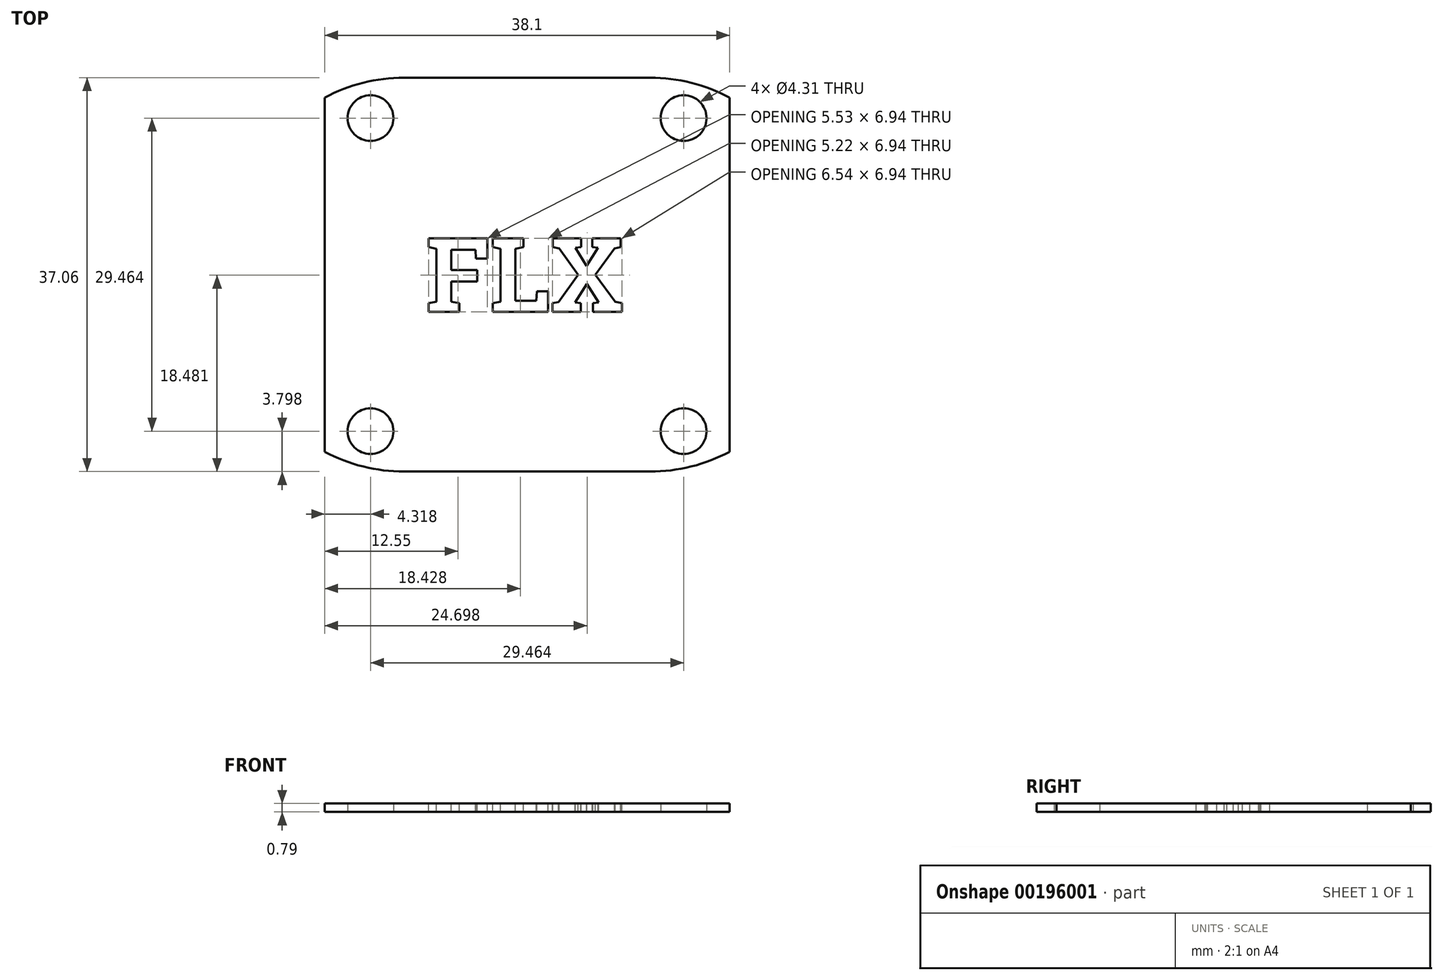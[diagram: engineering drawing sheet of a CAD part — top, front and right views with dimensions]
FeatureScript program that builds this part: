
annotation { "Feature Type Name" : "Feature", "Feature Type Description" : "" }
export const myFeature = defineFeature(function(context is Context, id is Id, definition is map)
    precondition{}
    {
        {
            var Q0;
            Q0=qCreatedBy(makeId("Top.planeOp"),FACE);
            var sketch = newSketch(context, id + "F0", { "sketchPlane" : qUnion([Q0])});
            skLineSegment(sketch, "E0", {"start": v(-19.05, 0) * mm, "end": v(-19.05, 16.67) * mm});
            skLineSegment(sketch, "E1", {"start": v(19.05, 0) * mm, "end": v(19.05, 16.67) * mm});
            skArc(sketch, "E2", {"start": v(-11.58, 18.53) * mm, "mid": v(-15.43, 18.06) * mm, "end": v(-19.05, 16.67) * mm});
            skArc(sketch, "E3", {"start": v(19.05, 16.67) * mm, "mid": v(15.43, 18.06) * mm, "end": v(11.58, 18.53) * mm});
            skLineSegment(sketch, "E4", {"start": v(-11.58, 18.53) * mm, "end": v(0, 18.53) * mm});
            skLineSegment(sketch, "E5", {"start": v(0, 18.53) * mm, "end": v(11.58, 18.53) * mm});
            skLineSegment(sketch, "E6", {"start": v(-39.62, 0) * mm, "end": v(36.58, 0) * mm, "construction": true});
            skLineSegment(sketch, "E7.MirrorCS", {"start": v(-19.05, 0) * mm, "end": v(-19.05, -16.67) * mm});
            skLineSegment(sketch, "E8.MirrorCS", {"start": v(19.05, 0) * mm, "end": v(19.05, -16.67) * mm});
            skLineSegment(sketch, "E9.MirrorCS", {"start": v(-11.58, -18.53) * mm, "end": v(0, -18.53) * mm});
            skLineSegment(sketch, "E10.MirrorCS", {"start": v(0, -18.53) * mm, "end": v(11.58, -18.53) * mm});
            skArc(sketch, "E11.MirrorCS", {"start": v(-11.58, -18.53) * mm, "mid": v(-15.43, -18.06) * mm, "end": v(-19.05, -16.67) * mm});
            skArc(sketch, "E12.MirrorCS", {"start": v(19.05, -16.67) * mm, "mid": v(15.43, -18.06) * mm, "end": v(11.58, -18.53) * mm});
            skCircle(sketch, "E13", {"center": v(-14.73, 14.73) * mm, "radius": 2.15 * mm});
            skCircle(sketch, "E14.MirrorC", {"center": v(-14.73, -14.73) * mm, "radius": 2.15 * mm});
            skLineSegment(sketch, "E15", {"start": v(0, 16.68) * mm, "end": v(0, -10.48) * mm, "construction": true});
            skCircle(sketch, "E16.MirrorC", {"center": v(14.73, 14.73) * mm, "radius": 2.15 * mm});
            skCircle(sketch, "E17.MirrorC", {"center": v(14.73, -14.73) * mm, "radius": 2.15 * mm});
            skSolve(sketch);
        }
        {
            var Q0;
            Q0=qSketchRegion(id+"F0",true);
            extrude(context, id + "F1", {"entities" : qUnion([Q0]), "depth" : 0.8 * mm});
        }
        {
            var Q0;
            Q0=makeQuery(id+"F1.opExtrude","CAP_FACE",FACE,{"disambiguationData":[OSD([sQuery(id+"F0.wireOp",EDGE,"E0"),sQuery(id+"F0.wireOp",EDGE,"E1"),sQuery(id+"F0.wireOp",EDGE,"E2"),sQuery(id+"F0.wireOp",EDGE,"E3"),sQuery(id+"F0.wireOp",EDGE,"E4"),sQuery(id+"F0.wireOp",EDGE,"E5"),sQuery(id+"F0.wireOp",EDGE,"E7.MirrorCS"),sQuery(id+"F0.wireOp",EDGE,"E8.MirrorCS"),sQuery(id+"F0.wireOp",EDGE,"E9.MirrorCS"),sQuery(id+"F0.wireOp",EDGE,"E10.MirrorCS"),sQuery(id+"F0.wireOp",EDGE,"E11.MirrorCS"),sQuery(id+"F0.wireOp",EDGE,"E12.MirrorCS"),sQuery(id+"F0.wireOp",EDGE,"E14.MirrorC"),sQuery(id+"F0.wireOp",EDGE,"E13"),sQuery(id+"F0.wireOp",EDGE,"E16.MirrorC"),sQuery(id+"F0.wireOp",EDGE,"E17.MirrorC")])],"isStart":false});
            var sketch = newSketch(context, id + "F2", { "sketchPlane" : qUnion([Q0])});
            skText(sketch, "E18", { "text": "FLX", "fontName": "RobotoSlab-Bold.ttf"});
            skLineSegment(sketch, "E19", {"start": v(9.52, 0) * mm, "end": v(-9.53, 0) * mm, "construction": true});
            const initialGuessF2  = {"E18": [-0.00953, -0.00352, 1, 0, 0.00703]};
            skSetInitialGuess(sketch, initialGuessF2);
            skSolve(sketch);
        }
        {
            var Q0;
            Q0=makeQuery(id+"F2.imprint","IMPRINT",FACE,{"disambiguationData":[TD([[makeQuery(id+"F2.imprint","IMPRINT",EDGE,{"derivedFrom":sQuery(id+"F2.wireOp",EDGE,"E18.sketch_text.stroke-34")}),-1.0]])]});
            var Q1;
            Q1=makeQuery(id+"F2.imprint","IMPRINT",FACE,{"disambiguationData":[TD([[makeQuery(id+"F2.imprint","IMPRINT",EDGE,{"derivedFrom":sQuery(id+"F2.wireOp",EDGE,"E18.sketch_text.stroke-18")}),-1.0]])]});
            var Q2;
            Q2=makeQuery(id+"F2.imprint","IMPRINT",FACE,{"disambiguationData":[TD([[makeQuery(id+"F2.imprint","IMPRINT",EDGE,{"derivedFrom":sQuery(id+"F2.wireOp",EDGE,"E18.sketch_text.stroke-0")}),-1.0]])]});
            extrude(context, id + "F3", {"entities" : qUnion([Q0, Q1, Q2]), "operationType" : NewBodyOperationType.REMOVE, "oppositeDirection" : true, "depth" : 25.4 * mm});
        }
    });
